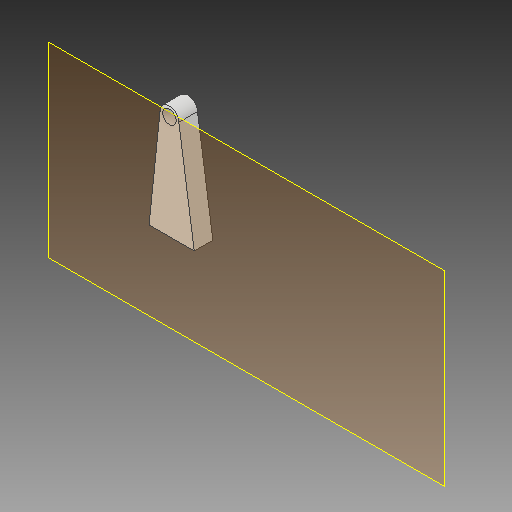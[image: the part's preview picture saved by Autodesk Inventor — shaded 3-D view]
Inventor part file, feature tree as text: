
AUTODESK INVENTOR PART (.ipt)
format: ipt  version: 2017 (Build 210142000, 142)  size: 87,552 bytes
history: native  units: in
note: dims shown in document units (in); Inventor stores cm internally (conversion verified against a paired STEP export)
features: other x3, sketch x1, plane x1
ambient origin geometry x8: Origin, YZ Plane, XZ Plane, XY Plane, X Axis, Y Axis, Z Axis, Center Point
bodies: Solid1 (feature_tree)
feature tree (5):
  other  "ARM.ipt"
  other  "Solid1::ARM.ipt"
  other  "TaggingFeature1"
  sketch  "Sketch1"  dims[d0=0.3937in]
  plane  "Work Plane1"
